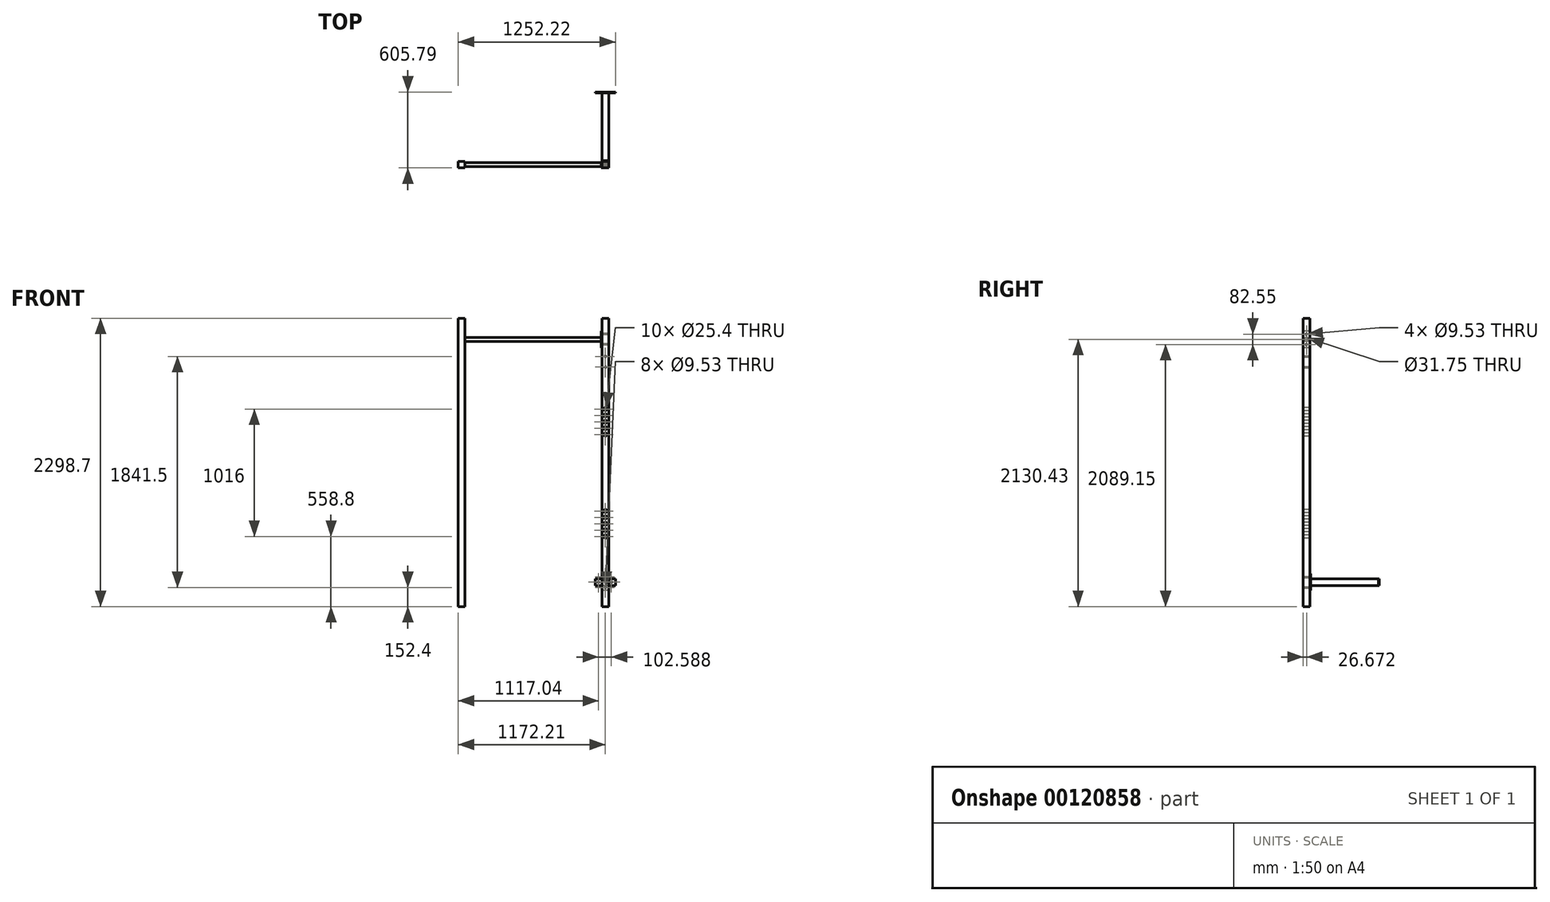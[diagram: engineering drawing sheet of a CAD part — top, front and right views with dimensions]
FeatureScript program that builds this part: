
annotation { "Feature Type Name" : "Feature", "Feature Type Description" : "" }
export const myFeature = defineFeature(function(context is Context, id is Id, definition is map)
    precondition{}
    {
        {
            var Q0;
            Q0=qCreatedBy(makeId("Top.planeOp"),FACE);
            var sketch = newSketch(context, id + "F0", { "sketchPlane" : qUnion([Q0])});
            skLineSegment(sketch, "E0.bottom", {"start": v(-520.75, 34.25) * mm, "end": v(-467.4, 34.25) * mm});
            skLineSegment(sketch, "E0.top", {"start": v(-520.75, -19.09) * mm, "end": v(-467.4, -19.09) * mm});
            skLineSegment(sketch, "E0.left", {"start": v(-520.75, 34.25) * mm, "end": v(-520.75, -19.09) * mm});
            skLineSegment(sketch, "E0.right", {"start": v(-467.4, 34.25) * mm, "end": v(-467.4, -19.09) * mm});
            skLineSegment(sketch, "E1.bottom", {"start": v(624.8, 34.25) * mm, "end": v(678.13, 34.25) * mm});
            skLineSegment(sketch, "E1.top", {"start": v(624.8, -19.09) * mm, "end": v(678.13, -19.09) * mm});
            skLineSegment(sketch, "E1.left", {"start": v(624.8, 34.25) * mm, "end": v(624.8, -19.09) * mm});
            skLineSegment(sketch, "E1.right", {"start": v(678.13, 34.25) * mm, "end": v(678.13, -19.09) * mm});
            skSolve(sketch);
        }
        {
            var Q0;
            Q0=makeQuery(id+"F0.imprint","IMPRINT",FACE,{"disambiguationData":[TD([[makeQuery(id+"F0.imprint","IMPRINT",EDGE,{"derivedFrom":sQuery(id+"F0.wireOp",EDGE,"E0.bottom")}),-1.0]])]});
            var Q1;
            Q1=makeQuery(id+"F0.imprint","IMPRINT",FACE,{"disambiguationData":[TD([[makeQuery(id+"F0.imprint","IMPRINT",EDGE,{"derivedFrom":sQuery(id+"F0.wireOp",EDGE,"E1.bottom")}),-1.0]])]});
            extrude(context, id + "F1", {"entities" : qUnion([Q0, Q1]), "depth" : 2298.7 * mm});
        }
        {
            var Q0;
            Q0=makeQuery(id+"F1.opExtrude","SWEPT_FACE",FACE,{"disambiguationData":[OSD([sQuery(id+"F0.wireOp",EDGE,"E1.bottom")])]});
            var sketch = newSketch(context, id + "F2", { "sketchPlane" : qUnion([Q0])});
            skLineSegment(sketch, "E2.bottom", {"start": v(-678.13, 221.46) * mm, "end": v(-624.8, 221.46) * mm});
            skLineSegment(sketch, "E2.top", {"start": v(-678.13, 168.12) * mm, "end": v(-624.8, 168.12) * mm});
            skLineSegment(sketch, "E2.left", {"start": v(-678.13, 221.46) * mm, "end": v(-678.13, 168.12) * mm});
            skLineSegment(sketch, "E2.right", {"start": v(-624.8, 221.46) * mm, "end": v(-624.8, 168.12) * mm});
            skLineSegment(sketch, "E3.bottom", {"start": v(-678.13, 261.46) * mm, "end": v(-624.8, 261.46) * mm});
            skLineSegment(sketch, "E3.top", {"start": v(-678.13, 128.11) * mm, "end": v(-624.8, 128.11) * mm});
            skLineSegment(sketch, "E3.left", {"start": v(-678.13, 261.46) * mm, "end": v(-678.13, 128.11) * mm});
            skLineSegment(sketch, "E3.right", {"start": v(-624.8, 261.46) * mm, "end": v(-624.8, 128.11) * mm});
            skPoint(sketch, "E4", {"position": v(-678.13, 194.79) * mm});
            skCircle(sketch, "E5", {"center": v(-651.46, 152.4) * mm, "radius": 4.76 * mm});
            skCircle(sketch, "E6", {"center": v(-651.46, 237.17) * mm, "radius": 4.76 * mm});
            skPoint(sketch, "E7", {"position": v(-651.46, 261.46) * mm});
            skPoint(sketch, "E8", {"position": v(-651.46, 128.11) * mm});
            skLineSegment(sketch, "E9", {"start": v(-651.46, 261.46) * mm, "end": v(-651.46, 237.17) * mm, "construction": true});
            skLineSegment(sketch, "E10", {"start": v(-651.46, 152.4) * mm, "end": v(-651.46, 128.11) * mm, "construction": true});
            skLineSegment(sketch, "E11.bottom", {"start": v(-678.13, 1978.18) * mm, "end": v(-624.8, 1978.18) * mm});
            skLineSegment(sketch, "E11.top", {"start": v(-678.13, 1924.84) * mm, "end": v(-624.8, 1924.84) * mm});
            skLineSegment(sketch, "E11.left", {"start": v(-678.13, 1978.18) * mm, "end": v(-678.13, 1924.84) * mm});
            skLineSegment(sketch, "E11.right", {"start": v(-624.8, 1978.18) * mm, "end": v(-624.8, 1924.84) * mm});
            skLineSegment(sketch, "E12.bottom", {"start": v(-678.13, 2018.19) * mm, "end": v(-624.8, 2018.19) * mm});
            skLineSegment(sketch, "E12.top", {"start": v(-678.13, 1884.84) * mm, "end": v(-624.8, 1884.84) * mm});
            skLineSegment(sketch, "E12.left", {"start": v(-678.13, 2018.19) * mm, "end": v(-678.13, 1884.84) * mm});
            skLineSegment(sketch, "E12.right", {"start": v(-624.8, 2018.19) * mm, "end": v(-624.8, 1884.84) * mm});
            skPoint(sketch, "E13", {"position": v(-678.13, 1951.51) * mm});
            skCircle(sketch, "E14", {"center": v(-651.46, 1909.13) * mm, "radius": 4.76 * mm});
            skCircle(sketch, "E15", {"center": v(-651.46, 1993.9) * mm, "radius": 4.76 * mm});
            skPoint(sketch, "E16", {"position": v(-651.46, 2018.19) * mm});
            skPoint(sketch, "E17", {"position": v(-651.46, 1884.84) * mm});
            skLineSegment(sketch, "E18", {"start": v(-651.46, 2018.19) * mm, "end": v(-651.46, 1993.9) * mm, "construction": true});
            skLineSegment(sketch, "E19", {"start": v(-651.46, 1909.13) * mm, "end": v(-651.46, 1884.84) * mm, "construction": true});
            skSolve(sketch);
        }
        {
            var Q0;
            {var subQ2=sQuery(id+"F2.wireOp",EDGE,"de5c0bc2-cd4f-4984-b90a-ed2ed7d31b32.bottom");Q0=makeQuery(id+"F2.imprint","IMPRINT",FACE,{"disambiguationData":[TD([[makeQuery(id+"F2.imprint","IMPRINT",EDGE,{"derivedFrom":subQ2}),1.0]])]});}
            var Q1;
            {var subQ0=sQuery(id+"F2.wireOp",EDGE,"de5c0bc2-cd4f-4984-b90a-ed2ed7d31b32.bottom");Q1=makeQuery(id+"F2.imprint","IMPRINT",FACE,{"disambiguationData":[TD([[makeQuery(id+"F2.imprint","IMPRINT",EDGE,{"derivedFrom":subQ0}),-1.0]])]});}
            var Q2;
            {var subQ0=sQuery(id+"F2.wireOp",EDGE,"E2.bottom");Q2=makeQuery(id+"F2.imprint","IMPRINT",FACE,{"disambiguationData":[TD([[makeQuery(id+"F2.imprint","IMPRINT",EDGE,{"derivedFrom":subQ0}),1.0]])]});}
            var Q3;
            {var subQ0=sQuery(id+"F2.wireOp",EDGE,"E2.bottom");Q3=makeQuery(id+"F2.imprint","IMPRINT",FACE,{"disambiguationData":[TD([[makeQuery(id+"F2.imprint","IMPRINT",EDGE,{"derivedFrom":subQ0}),-1.0]])]});}
            var Q4;
            {var subQ0=sQuery(id+"F2.wireOp",EDGE,"E2.top");Q4=makeQuery(id+"F2.imprint","IMPRINT",FACE,{"disambiguationData":[TD([[makeQuery(id+"F2.imprint","IMPRINT",EDGE,{"derivedFrom":subQ0}),-1.0]])]});}
            extrude(context, id + "F3", {"entities" : qUnion([Q0, Q1, Q2, Q3, Q4]), "depth" : 6.35 * mm});
        }
        {
            var Q0;
            {var subQ0=sQuery(id+"F2.wireOp",EDGE,"de5c0bc2-cd4f-4984-b90a-ed2ed7d31b32.bottom");Q0=makeQuery(id+"F2.imprint","IMPRINT",FACE,{"disambiguationData":[TD([[makeQuery(id+"F2.imprint","IMPRINT",EDGE,{"derivedFrom":subQ0}),-1.0]])]});}
            var Q1;
            {var subQ0=sQuery(id+"F2.wireOp",EDGE,"E2.bottom");Q1=makeQuery(id+"F2.imprint","IMPRINT",FACE,{"disambiguationData":[TD([[makeQuery(id+"F2.imprint","IMPRINT",EDGE,{"derivedFrom":subQ0}),-1.0]])]});}
            extrude(context, id + "F4", {"entities" : qUnion([Q0, Q1]), "depth" : 546.1 * mm});
        }
        {
            var Q0;
            Q0=makeQuery(id+"F4.opExtrude","CAP_FACE",FACE,{"disambiguationData":[OSD([sQuery(id+"F2.wireOp",EDGE,"E2.bottom"),sQuery(id+"F2.wireOp",EDGE,"E2.top"),sQuery(id+"F2.wireOp",EDGE,"E3.left"),sQuery(id+"F2.wireOp",EDGE,"E3.right")])],"isStart":false});
            var sketch = newSketch(context, id + "F5", { "sketchPlane" : qUnion([Q0])});
            skLineSegment(sketch, "E20.bottom", {"start": v(-731.47, 221.46) * mm, "end": v(-571.45, 221.46) * mm});
            skLineSegment(sketch, "E20.top", {"start": v(-731.47, 168.12) * mm, "end": v(-571.45, 168.12) * mm});
            skLineSegment(sketch, "E20.left", {"start": v(-731.47, 221.46) * mm, "end": v(-731.47, 168.12) * mm});
            skLineSegment(sketch, "E20.right", {"start": v(-571.45, 221.46) * mm, "end": v(-571.45, 168.12) * mm});
            skPoint(sketch, "E21", {"position": v(-731.47, 194.79) * mm});
            skPoint(sketch, "E22", {"position": v(-678.13, 194.79) * mm});
            skPoint(sketch, "E23", {"position": v(-651.46, 221.46) * mm});
            skCircle(sketch, "E24", {"center": v(-596.29, 194.79) * mm, "radius": 4.76 * mm});
            skCircle(sketch, "E25", {"center": v(-698.88, 194.79) * mm, "radius": 4.76 * mm});
            skSolve(sketch);
        }
        {
            var Q0;
            Q0 = qSketchRegion(id + "F5", true);
            extrude(context, id + "F6", {"entities" : qUnion([Q0]), "depth" : 6.35 * mm});
        }
        {
            var Q0;
            Q0=makeQuery(id+"F2.imprint","IMPRINT",FACE,{"disambiguationData":[TD([[makeQuery(id+"F2.imprint","IMPRINT",EDGE,{"derivedFrom":sQuery(id+"F2.wireOp",EDGE,"E6")}),1.0]])]});
            var Q1;
            Q1=makeQuery(id+"F2.imprint","IMPRINT",FACE,{"disambiguationData":[TD([[makeQuery(id+"F2.imprint","IMPRINT",EDGE,{"derivedFrom":sQuery(id+"F2.wireOp",EDGE,"E5")}),1.0]])]});
            var Q2;
            Q2=makeQuery(id+"F2.imprint","IMPRINT",FACE,{"disambiguationData":[TD([[makeQuery(id+"F2.imprint","IMPRINT",EDGE,{"derivedFrom":sQuery(id+"F2.wireOp",EDGE,"E15")}),1.0]])]});
            var Q3;
            Q3=makeQuery(id+"F2.imprint","IMPRINT",FACE,{"disambiguationData":[TD([[makeQuery(id+"F2.imprint","IMPRINT",EDGE,{"derivedFrom":sQuery(id+"F2.wireOp",EDGE,"E14")}),1.0]])]});
            extrude(context, id + "F7", {"entities" : qUnion([Q0, Q1, Q2, Q3]), "operationType" : NewBodyOperationType.REMOVE, "endBound" : BoundingType.THROUGH_ALL, "oppositeDirection" : true, "depth" : 25.4 * mm});
        }
        {
            var Q0;
            Q0=makeQuery(id+"F1.opExtrude","SWEPT_FACE",FACE,{"disambiguationData":[OSD([sQuery(id+"F0.wireOp",EDGE,"E1.left")])]});
            var sketch = newSketch(context, id + "F8", { "sketchPlane" : qUnion([Q0])});
            skLineSegment(sketch, "E26.0", {"start": v(19.09, 2298.7) * mm, "end": v(19.09, 0) * mm});
            skLineSegment(sketch, "E27.bottom", {"start": v(-34.25, 2197.1) * mm, "end": v(19.09, 2197.1) * mm});
            skLineSegment(sketch, "E27.top", {"start": v(-34.25, 2063.75) * mm, "end": v(19.09, 2063.75) * mm});
            skLineSegment(sketch, "E27.left", {"start": v(19.09, 2197.1) * mm, "end": v(19.09, 2063.75) * mm});
            skLineSegment(sketch, "E27.right", {"start": v(-34.25, 2197.1) * mm, "end": v(-34.25, 2063.75) * mm});
            skPoint(sketch, "E28", {"position": v(19.09, 2130.43) * mm});
            skPoint(sketch, "E29", {"position": v(-7.58, 2197.1) * mm});
            skCircle(sketch, "E30", {"center": v(-7.58, 2130.43) * mm, "radius": 15.88 * mm});
            skCircle(sketch, "E31", {"center": v(-7.58, 2171.7) * mm, "radius": 4.76 * mm});
            skCircle(sketch, "E32", {"center": v(-7.58, 2089.15) * mm, "radius": 4.76 * mm});
            skLineSegment(sketch, "E33", {"start": v(-7.58, 2130.43) * mm, "end": v(-7.58, 2171.7) * mm, "construction": true});
            skLineSegment(sketch, "E34", {"start": v(-7.58, 2130.43) * mm, "end": v(-7.58, 2089.15) * mm, "construction": true});
            skSolve(sketch);
        }
        {
            var Q0;
            Q0=makeQuery(id+"F8.imprint","IMPRINT",FACE,{"disambiguationData":[TD([[makeQuery(id+"F8.imprint","IMPRINT",EDGE,{"derivedFrom":sQuery(id+"F8.wireOp",EDGE,"E27.bottom")}),-1.0]])]});
            extrude(context, id + "F9", {"entities" : qUnion([Q0]), "depth" : 6.35 * mm});
        }
        {
            var Q0;
            Q0=makeQuery(id+"F8.imprint","IMPRINT",FACE,{"disambiguationData":[TD([[makeQuery(id+"F8.imprint","IMPRINT",EDGE,{"derivedFrom":sQuery(id+"F8.wireOp",EDGE,"E30")}),1.0]])]});
            extrude(context, id + "F10", {"entities" : qUnion([Q0]), "endBound" : BoundingType.UP_TO_NEXT, "depth" : 25.4 * mm});
        }
        {
            var Q0;
            Q0=makeQuery(id+"F8.imprint","IMPRINT",FACE,{"disambiguationData":[TD([[makeQuery(id+"F8.imprint","IMPRINT",EDGE,{"derivedFrom":sQuery(id+"F8.wireOp",EDGE,"E31")}),1.0]])]});
            var Q1;
            Q1=makeQuery(id+"F8.imprint","IMPRINT",FACE,{"disambiguationData":[TD([[makeQuery(id+"F8.imprint","IMPRINT",EDGE,{"derivedFrom":sQuery(id+"F8.wireOp",EDGE,"E32")}),1.0]])]});
            extrude(context, id + "F11", {"entities" : qUnion([Q0, Q1]), "operationType" : NewBodyOperationType.REMOVE, "endBound" : BoundingType.THROUGH_ALL, "oppositeDirection" : true, "depth" : 25.4 * mm});
        }
        {
            var Q0;
            Q0=makeQuery(id+"F1.opExtrude","SWEPT_FACE",FACE,{"disambiguationData":[OSD([sQuery(id+"F0.wireOp",EDGE,"E1.top")])]});
            var sketch = newSketch(context, id + "F12", { "sketchPlane" : qUnion([Q0])});
            skCircle(sketch, "E35", {"center": v(651.46, 558.8) * mm, "radius": 12.7 * mm});
            skPoint(sketch, "E36.0", {"position": v(651.46, 237.17) * mm});
            skPoint(sketch, "E37.0", {"position": v(651.46, 261.46) * mm});
            skCircle(sketch, "E38.0.1.0", {"center": v(651.46, 609.6) * mm, "radius": 12.7 * mm});
            skCircle(sketch, "E38.0.2.0", {"center": v(651.46, 660.4) * mm, "radius": 12.7 * mm});
            skCircle(sketch, "E38.0.3.0", {"center": v(651.46, 711.2) * mm, "radius": 12.7 * mm});
            skCircle(sketch, "E38.0.4.0", {"center": v(651.46, 762) * mm, "radius": 12.7 * mm});
            skLineSegment(sketch, "E38.direction1", {"start": v(651.46, 558.8) * mm, "end": v(673.06, 558.8) * mm, "construction": true});
            skLineSegment(sketch, "E38.direction2", {"start": v(651.46, 558.8) * mm, "end": v(651.46, 609.6) * mm, "construction": true});
            skCircle(sketch, "E39", {"center": v(651.46, 1371.6) * mm, "radius": 12.7 * mm});
            skCircle(sketch, "E40.0.1.0", {"center": v(651.46, 1422.4) * mm, "radius": 12.7 * mm});
            skCircle(sketch, "E40.0.2.0", {"center": v(651.46, 1473.2) * mm, "radius": 12.7 * mm});
            skCircle(sketch, "E40.0.3.0", {"center": v(651.46, 1524) * mm, "radius": 12.7 * mm});
            skCircle(sketch, "E40.0.4.0", {"center": v(651.46, 1574.8) * mm, "radius": 12.7 * mm});
            skLineSegment(sketch, "E40.direction1", {"start": v(651.46, 1371.6) * mm, "end": v(669.52, 1371.6) * mm, "construction": true});
            skLineSegment(sketch, "E40.direction2", {"start": v(651.46, 1371.6) * mm, "end": v(651.46, 1422.4) * mm, "construction": true});
            skPoint(sketch, "E41", {"position": v(651.46, 2298.7) * mm});
            skSolve(sketch);
        }
        {
            var Q0;
            Q0 = qSketchRegion(id + "F12", true);
            extrude(context, id + "F13", {"entities" : qUnion([Q0]), "operationType" : NewBodyOperationType.REMOVE, "endBound" : BoundingType.THROUGH_ALL, "oppositeDirection" : true, "depth" : 25.4 * mm});
        }
    });
